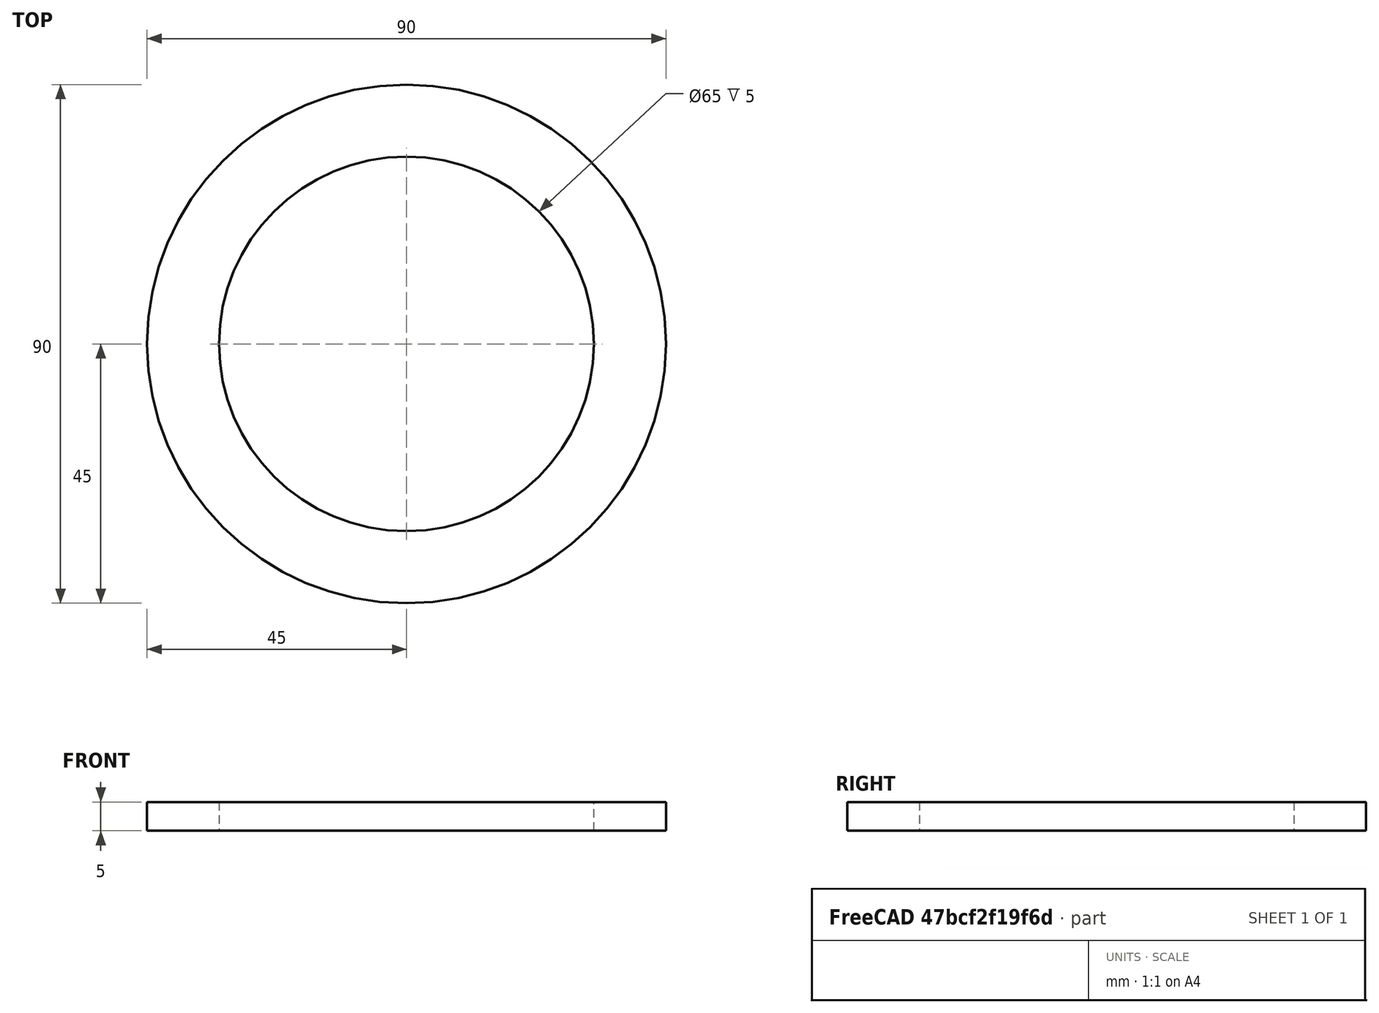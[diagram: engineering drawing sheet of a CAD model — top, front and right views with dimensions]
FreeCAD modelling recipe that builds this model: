
FCSTD DOCUMENT  (FreeCAD 0.19R24276 (Git))
Label: THRUST-65-90
License: All rights reserved
LicenseURL: http://en.wikipedia.org/wiki/All_rights_reserved
objects: PartDesign::CoordinateSystem×1, Sketcher::SketchObject×1, PartDesign::Pad×1, PartDesign::Body×1, App::Part×1
note: 5 computed .brp shape members not serialized (recipe doc carries the construction recipe); baked Part::Feature solids carry a one-line shape summary decoded from their .brp

FEATURE [PartDesign::CoordinateSystem] LCS_0002
  AttacherType = Attacher::AttachEngine3D
  MapMode = 2
  Support = -> [X_Axis005]
FEATURE [Sketcher::SketchObject] Sketch008
  FullyConstrained = false
  MapMode = 5
  Support = -> [XY_Plane006]
  sketch-geometry (2):
    g0: Circle CenterX=0 CenterY=0 CenterZ=0 NormalX=0 NormalY=0 NormalZ=1 AngleXU=0 Radius=32.5
    g1: Circle CenterX=0 CenterY=0 CenterZ=0 NormalX=0 NormalY=0 NormalZ=1 AngleXU=0 Radius=45
  constraints (4):
    c: Coincident(g0,g-1)
    c: Coincident(g0,g1)
    c: Diameter(g1) = 90
    c: Diameter(g0) = 65
FEATURE [PartDesign::Pad] Pad007
  AllowMultiFace = false
  Direction = (1,1,1)
  Length = 5
  Length2 = 100
  Profile = -> Sketch008
  Type = 0
FEATURE [PartDesign::Body] Body002
  Group = -> [Sketch008,Pad007]
  Origin = -> Origin006
  Tip = -> Pad007
FEATURE [App::Part] THRUST_65_90
  Group = -> [LCS_0002,Body002]
  Origin = -> Origin005
